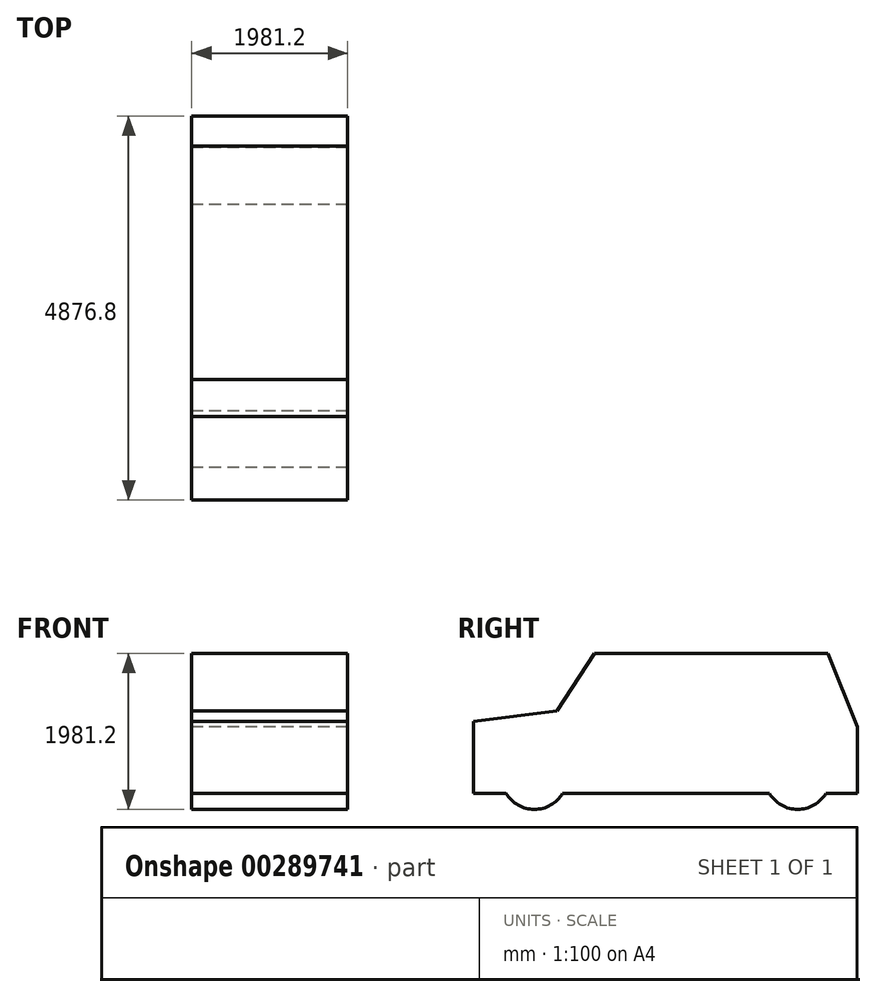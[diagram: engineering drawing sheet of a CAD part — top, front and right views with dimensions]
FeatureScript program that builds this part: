
annotation { "Feature Type Name" : "Feature", "Feature Type Description" : "" }
export const myFeature = defineFeature(function(context is Context, id is Id, definition is map)
    precondition{}
    {
        {
            var Q0;
            Q0=qCreatedBy(makeId("Top.planeOp"),FACE);
            var sketch = newSketch(context, id + "F0", { "sketchPlane" : qUnion([Q0])});
            skLineSegment(sketch, "E0.bottom", {"start": v(990.6, -2438.4) * mm, "end": v(-990.6, -2438.4) * mm});
            skLineSegment(sketch, "E0.top", {"start": v(990.6, 2438.4) * mm, "end": v(-990.6, 2438.4) * mm});
            skLineSegment(sketch, "E0.left", {"start": v(990.6, -2438.4) * mm, "end": v(990.6, 2438.4) * mm});
            skLineSegment(sketch, "E0.right", {"start": v(-990.6, -2438.4) * mm, "end": v(-990.6, 2438.4) * mm});
            skPoint(sketch, "E0.middle", {"position": v(0, 0) * mm});
            skSolve(sketch);
        }
        {
            var Q0;
            Q0=makeQuery(id+"F0.imprint","IMPRINT",FACE,{"disambiguationData":[TD([[makeQuery(id+"F0.imprint","IMPRINT",EDGE,{"derivedFrom":sQuery(id+"F0.wireOp",EDGE,"E0.bottom")}),-1.0]])]});
            extrude(context, id + "F1", {"entities" : qUnion([Q0]), "depth" : 3048 * mm, "offsetDistance" : 30.48 * mm});
        }
        {
            var Q0;
            Q0=makeQuery(id+"F1.opExtrude","SWEPT_FACE",FACE,{"disambiguationData":[OSD([sQuery(id+"F0.wireOp",EDGE,"E0.right")])]});
            var sketch = newSketch(context, id + "F2", { "sketchPlane" : qUnion([Q0])});
            skLineSegment(sketch, "E1", {"start": v(2438.4, 1117.6) * mm, "end": v(1379.87, 1250.2) * mm});
            skLineSegment(sketch, "E2", {"start": v(1379.87, 1250.2) * mm, "end": v(907.7, 1981.2) * mm});
            skLineSegment(sketch, "E3", {"start": v(907.7, 1981.2) * mm, "end": v(-2060.41, 1981.2) * mm});
            skLineSegment(sketch, "E4", {"start": v(-2060.41, 1981.2) * mm, "end": v(-2438.4, 1045.64) * mm});
            skLineSegment(sketch, "E5", {"start": v(2438.4, 203.2) * mm, "end": v(-2438.4, 203.2) * mm});
            skCircle(sketch, "E6", {"center": v(-1676.52, 419.1) * mm, "radius": 419.1 * mm});
            skCircle(sketch, "E7", {"center": v(1667.85, 419.1) * mm, "radius": 419.1 * mm});
            skSolve(sketch);
        }
        {
            var Q0;
            {var subQ1=sQuery(id+"F2.wireOp",EDGE,"E1");Q0=makeQuery(id+"F2.imprint","IMPRINT",FACE,{"disambiguationData":[TD([[makeQuery(id+"F2.imprint","IMPRINT",EDGE,{"derivedFrom":subQ1}),-1.0]])]});}
            var Q1;
            {var subQ0=sQuery(id+"F2.wireOp",EDGE,"E5");var subQ4=sQuery(id+"F2.wireOp",EDGE,"E6");var subQ5=makeQuery(id+"F2.imprint","INTERSECT",VERTEX,{"disambiguationData":[OD(1.0)],"derivedFrom":[subQ0,subQ4]});Q1=makeQuery(id+"F2.imprint","IMPRINT",FACE,{"disambiguationData":[TD([[makeQuery(id+"F2.imprint","IMPRINT",EDGE,{"disambiguationData":[TD([[subQ5,-1.0]])],"derivedFrom":subQ4}),-1.0]])]});}
            var Q2;
            {var subQ0=sQuery(id+"F2.wireOp",EDGE,"E7");var subQ1=sQuery(id+"F2.wireOp",EDGE,"E5");var subQ2=makeQuery(id+"F2.imprint","INTERSECT",VERTEX,{"disambiguationData":[OD(0.0)],"derivedFrom":[subQ1,subQ0]});Q2=makeQuery(id+"F2.imprint","IMPRINT",FACE,{"disambiguationData":[TD([[makeQuery(id+"F2.imprint","IMPRINT",EDGE,{"disambiguationData":[TD([[subQ2,-1.0]])],"derivedFrom":subQ1}),1.0]])]});}
            var Q3;
            {var subQ0=sQuery(id+"F2.wireOp",EDGE,"E7");var subQ1=sQuery(id+"F2.wireOp",EDGE,"E5");var subQ2=makeQuery(id+"F2.imprint","INTERSECT",VERTEX,{"disambiguationData":[OD(1.0)],"derivedFrom":[subQ1,subQ0]});Q3=makeQuery(id+"F2.imprint","IMPRINT",FACE,{"disambiguationData":[TD([[makeQuery(id+"F2.imprint","IMPRINT",EDGE,{"disambiguationData":[TD([[subQ2,1.0]])],"derivedFrom":subQ0}),-1.0]])]});}
            extrude(context, id + "F3", {"entities" : qUnion([Q0, Q1, Q2, Q3]), "operationType" : NewBodyOperationType.REMOVE, "oppositeDirection" : true, "depth" : 6096 * mm, "offsetDistance" : 30.48 * mm});
        }
    });
